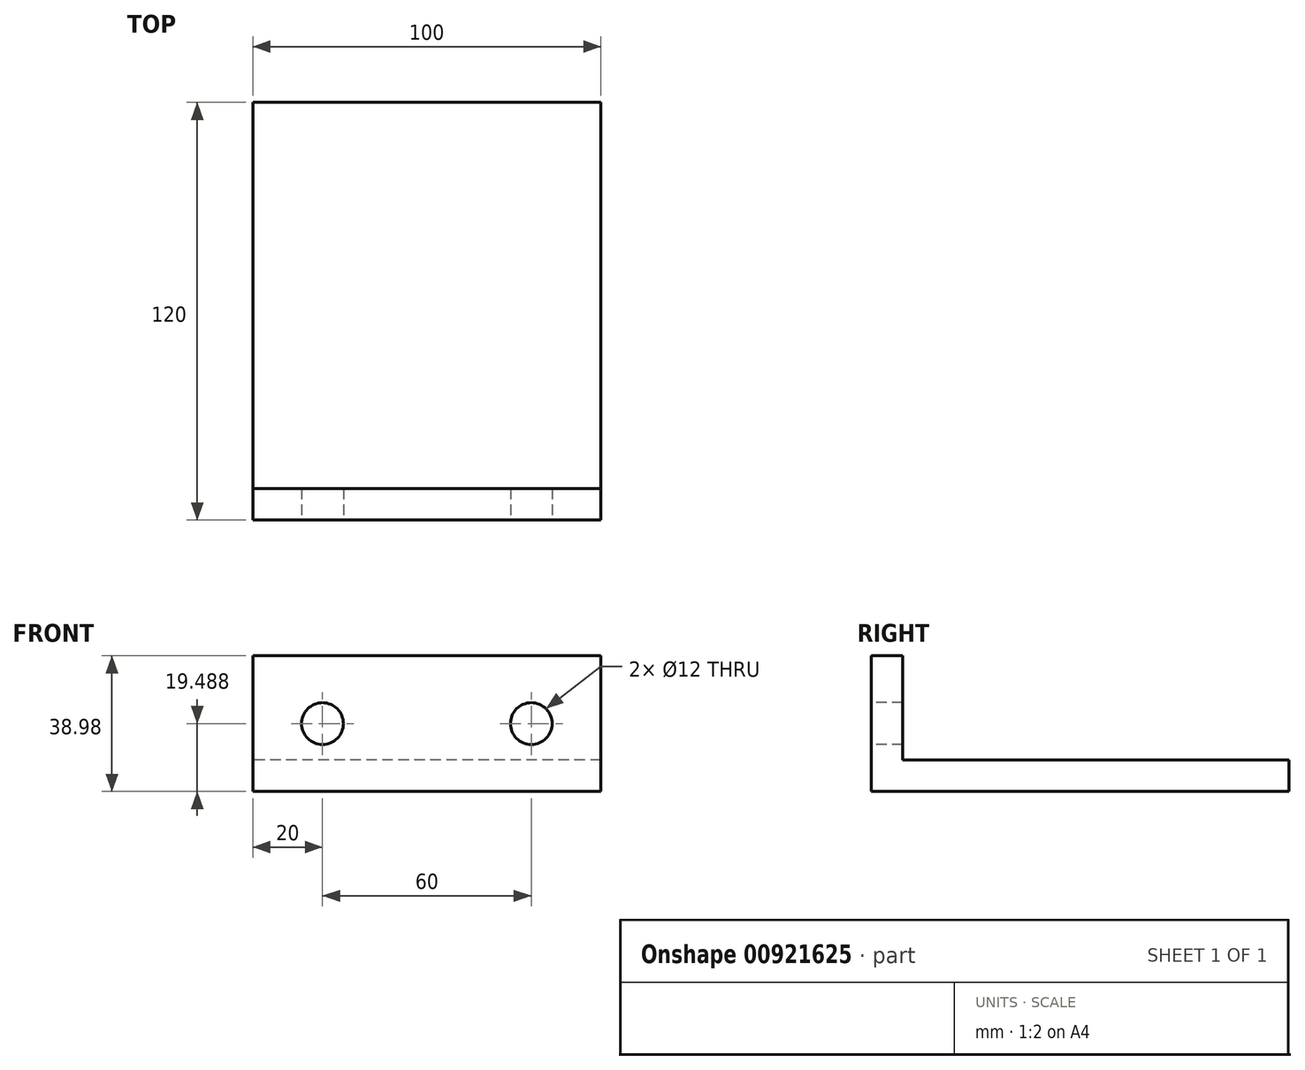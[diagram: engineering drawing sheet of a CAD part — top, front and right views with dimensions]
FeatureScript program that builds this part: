
annotation { "Feature Type Name" : "Feature", "Feature Type Description" : "" }
export const myFeature = defineFeature(function(context is Context, id is Id, definition is map)
    precondition{}
    {
        {
            var Q0;
            Q0=qCreatedBy(makeId("Right.planeOp"),FACE);
            var sketch = newSketch(context, id + "F0", { "sketchPlane" : qUnion([Q0])});
            skLineSegment(sketch, "E0", {"start": v(0, 0) * mm, "end": v(0, -38.98) * mm});
            skLineSegment(sketch, "E1", {"start": v(0, -38.98) * mm, "end": v(120, -38.98) * mm});
            skLineSegment(sketch, "E2", {"start": v(120, -38.98) * mm, "end": v(120, -29.98) * mm});
            skLineSegment(sketch, "E3", {"start": v(120, -29.98) * mm, "end": v(9, -29.98) * mm});
            skLineSegment(sketch, "E4", {"start": v(9, -29.98) * mm, "end": v(9, 0) * mm});
            skLineSegment(sketch, "E5", {"start": v(9, 0) * mm, "end": v(0, 0) * mm});
            skSolve(sketch);
        }
        {
            var Q0;
            Q0 = qSketchRegion(id + "F0", true);
            extrude(context, id + "F1", {"entities" : qUnion([Q0]), "depth" : 100 * mm, "offsetDistance" : 25 * mm});
        }
        {
            var Q0;
            Q0=makeQuery(id+"F1.opExtrude","SWEPT_FACE",FACE,{"disambiguationData":[OSD([sQuery(id+"F0.wireOp",EDGE,"E0")])]});
            var sketch = newSketch(context, id + "F2", { "sketchPlane" : qUnion([Q0])});
            skCircle(sketch, "E6", {"center": v(20, -19.5) * mm, "radius": 6 * mm});
            skPoint(sketch, "E6.centerSnap0", {"position": v(0, -19.5) * mm});
            skCircle(sketch, "E7", {"center": v(80, -19.5) * mm, "radius": 6 * mm});
            skPoint(sketch, "E7.centerSnap0", {"position": v(100, -19.5) * mm});
            skSolve(sketch);
        }
        {
            var Q0;
            Q0 = qSketchRegion(id + "F2", true);
            var Q1;
            Q1 = qBodyType(qCreatedBy(id + "F2" ,EDGE), BodyType.WIRE);
            extrude(context, id + "F3", {"entities" : qUnion([Q0]), "operationType" : NewBodyOperationType.REMOVE, "surfaceEntities" : qUnion([Q1]), "oppositeDirection" : true, "depth" : 25 * mm, "offsetDistance" : 25 * mm});
        }
    });
